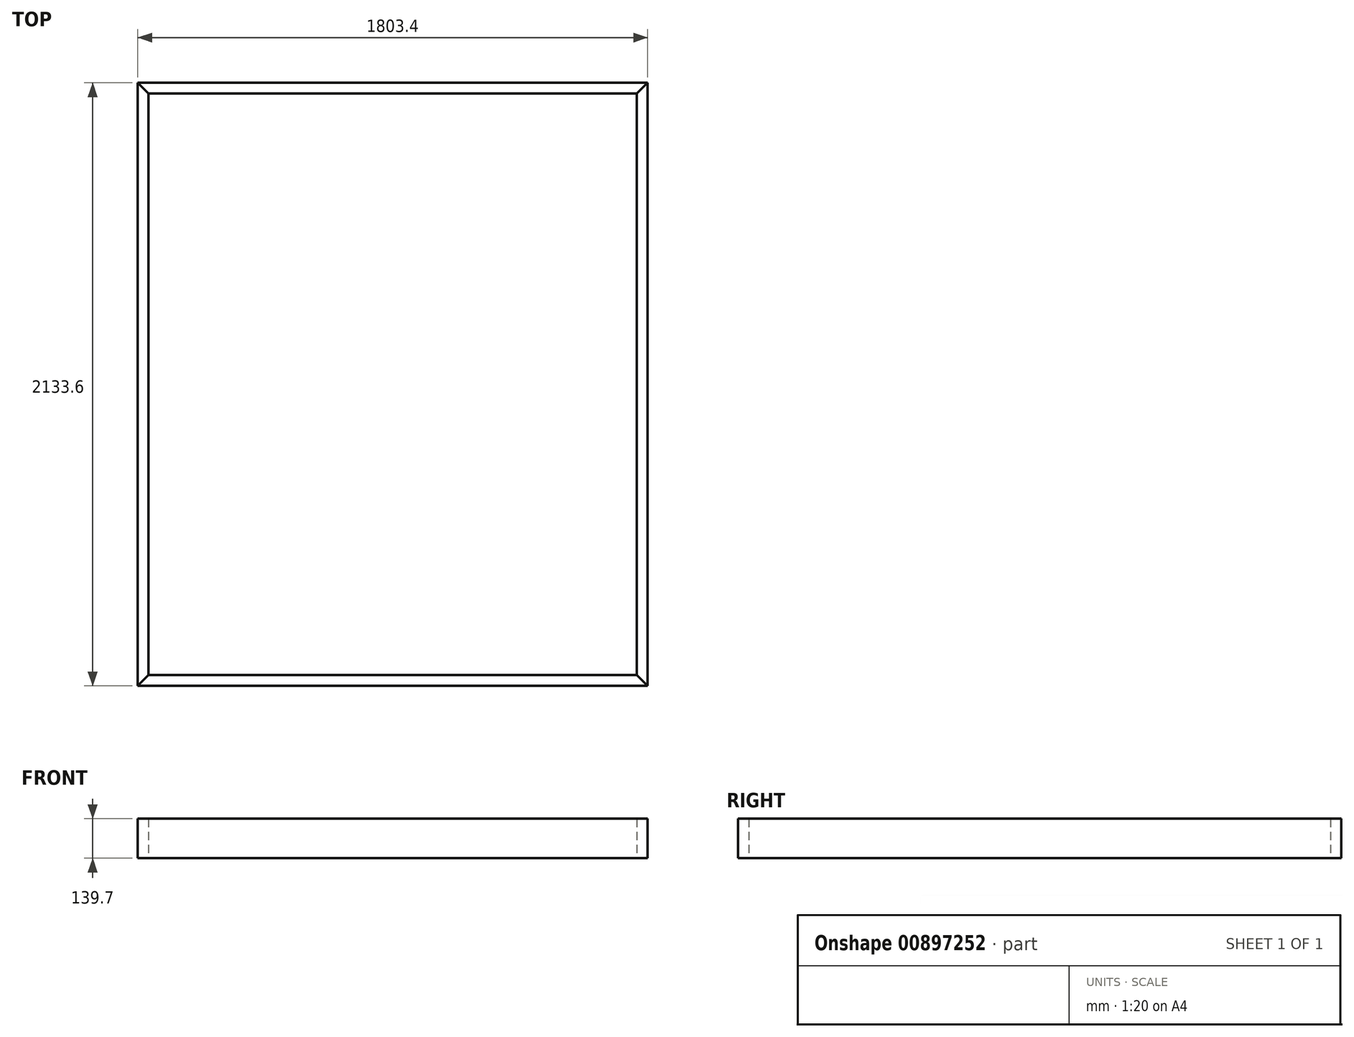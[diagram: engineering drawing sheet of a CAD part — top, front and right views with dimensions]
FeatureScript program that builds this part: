
annotation { "Feature Type Name" : "Feature", "Feature Type Description" : "" }
export const myFeature = defineFeature(function(context is Context, id is Id, definition is map)
    precondition{}
    {
        {
            var Q0;
            Q0=qCreatedBy(makeId("Top.planeOp"),FACE);
            var sketch = newSketch(context, id + "F0", { "sketchPlane" : qUnion([Q0])});
            skLineSegment(sketch, "E0.bottom", {"start": v(863.6, 1028.7) * mm, "end": v(-863.6, 1028.7) * mm});
            skLineSegment(sketch, "E0.top", {"start": v(863.6, -1028.7) * mm, "end": v(-863.6, -1028.7) * mm});
            skLineSegment(sketch, "E0.left", {"start": v(863.6, 1028.7) * mm, "end": v(863.6, -1028.7) * mm});
            skLineSegment(sketch, "E0.right", {"start": v(-863.6, 1028.7) * mm, "end": v(-863.6, -1028.7) * mm});
            skPoint(sketch, "E0.middle", {"position": v(0, 0) * mm});
            skLineSegment(sketch, "E1.bottom", {"start": v(-901.7, 1066.8) * mm, "end": v(901.7, 1066.8) * mm});
            skLineSegment(sketch, "E1.top", {"start": v(-901.7, -1066.8) * mm, "end": v(901.7, -1066.8) * mm});
            skLineSegment(sketch, "E1.left", {"start": v(-901.7, 1066.8) * mm, "end": v(-901.7, -1066.8) * mm});
            skLineSegment(sketch, "E1.right", {"start": v(901.7, 1066.8) * mm, "end": v(901.7, -1066.8) * mm});
            skLineSegment(sketch, "E2", {"start": v(-901.7, 1066.8) * mm, "end": v(-863.6, 1028.7) * mm});
            skLineSegment(sketch, "E3", {"start": v(901.7, 1066.8) * mm, "end": v(863.6, 1028.7) * mm});
            skLineSegment(sketch, "E4", {"start": v(901.7, -1066.8) * mm, "end": v(863.6, -1028.7) * mm});
            skLineSegment(sketch, "E5", {"start": v(-901.7, -1066.8) * mm, "end": v(-863.6, -1028.7) * mm});
            skSolve(sketch);
        }
        {
            var Q0;
            Q0=makeQuery(id+"F0.imprint","IMPRINT",FACE,{"disambiguationData":[TD([[makeQuery(id+"F0.imprint","IMPRINT",EDGE,{"derivedFrom":sQuery(id+"F0.wireOp",EDGE,"E0.bottom")}),-1.0]])]});
            var Q1;
            Q1=makeQuery(id+"F0.imprint","IMPRINT",FACE,{"disambiguationData":[TD([[makeQuery(id+"F0.imprint","IMPRINT",EDGE,{"derivedFrom":sQuery(id+"F0.wireOp",EDGE,"E0.top")}),1.0]])]});
            extrude(context, id + "F1", {"entities" : qUnion([Q0, Q1]), "depth" : 139.7 * mm, "offsetDistance" : 25.4 * mm});
        }
        {
            var Q0;
            Q0=makeQuery(id+"F0.imprint","IMPRINT",FACE,{"disambiguationData":[TD([[makeQuery(id+"F0.imprint","IMPRINT",EDGE,{"derivedFrom":sQuery(id+"F0.wireOp",EDGE,"E0.left")}),1.0]])]});
            var Q1;
            Q1=makeQuery(id+"F0.imprint","IMPRINT",FACE,{"disambiguationData":[TD([[makeQuery(id+"F0.imprint","IMPRINT",EDGE,{"derivedFrom":sQuery(id+"F0.wireOp",EDGE,"E0.right")}),-1.0]])]});
            extrude(context, id + "F2", {"entities" : qUnion([Q0, Q1]), "depth" : 139.7 * mm, "offsetDistance" : 25.4 * mm});
        }
    });
